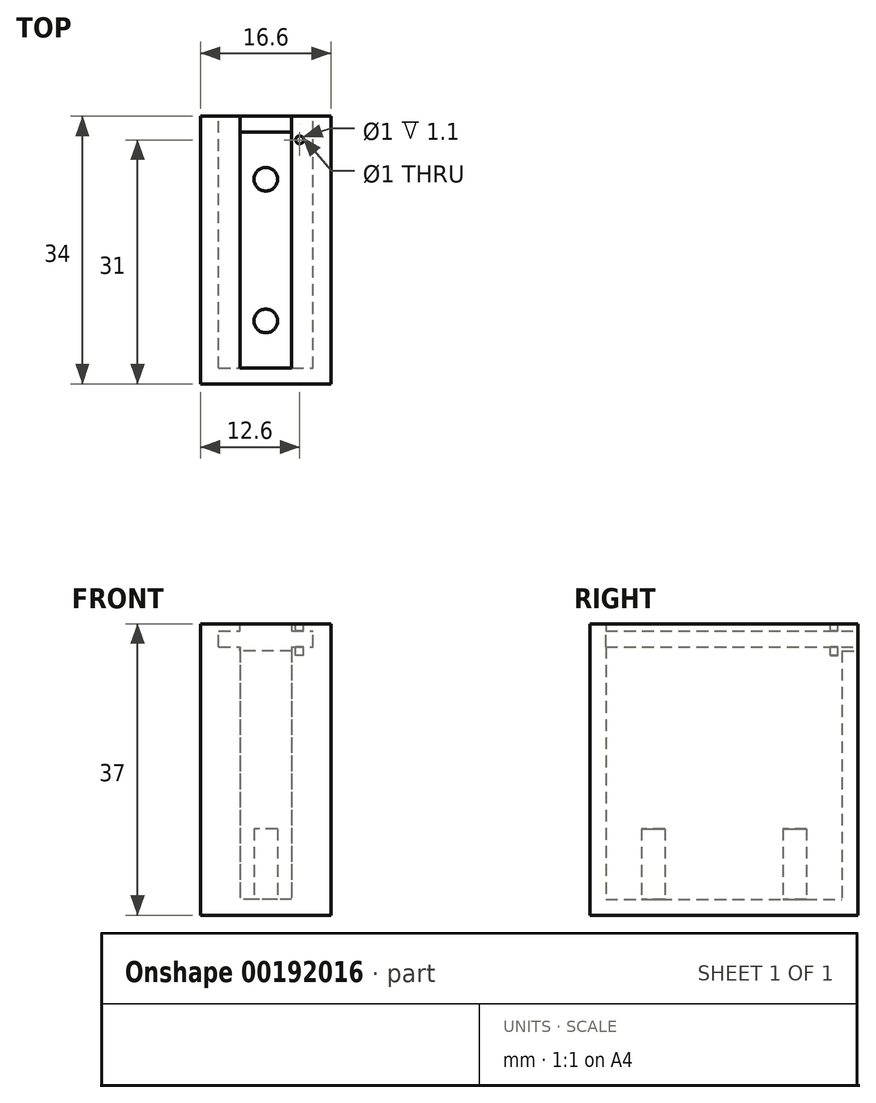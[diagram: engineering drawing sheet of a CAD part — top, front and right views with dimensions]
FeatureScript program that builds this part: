
annotation { "Feature Type Name" : "Feature", "Feature Type Description" : "" }
export const myFeature = defineFeature(function(context is Context, id is Id, definition is map)
    precondition{}
    {
        {
            var Q0;
            Q0=qCreatedBy(makeId("Top.planeOp"),FACE);
            var sketch = newSketch(context, id + "F0", { "sketchPlane" : qUnion([Q0])});
            skLineSegment(sketch, "E0.bottom", {"start": v(3.3, -15) * mm, "end": v(-3.3, -15) * mm});
            skLineSegment(sketch, "E0.top", {"start": v(3.3, 15) * mm, "end": v(-3.3, 15) * mm});
            skLineSegment(sketch, "E0.left", {"start": v(3.3, -15) * mm, "end": v(3.3, 15) * mm});
            skLineSegment(sketch, "E0.right", {"start": v(-3.3, -15) * mm, "end": v(-3.3, 15) * mm});
            skPoint(sketch, "E0.middle", {"position": v(0, 0) * mm});
            skLineSegment(sketch, "E1.bottom", {"start": v(-8.3, 17) * mm, "end": v(8.3, 17) * mm});
            skLineSegment(sketch, "E1.top", {"start": v(-8.3, -17) * mm, "end": v(8.3, -17) * mm});
            skLineSegment(sketch, "E1.left", {"start": v(-8.3, 17) * mm, "end": v(-8.3, -17) * mm});
            skLineSegment(sketch, "E1.right", {"start": v(8.3, 17) * mm, "end": v(8.3, -17) * mm});
            skSolve(sketch);
        }
        {
            var Q0;
            Q0=makeQuery(id+"F0.imprint","IMPRINT",FACE,{"disambiguationData":[TD([[makeQuery(id+"F0.imprint","IMPRINT",EDGE,{"derivedFrom":sQuery(id+"F0.wireOp",EDGE,"E0.bottom")}),-1.0]])]});
            extrude(context, id + "F1", {"entities" : qUnion([Q0]), "depth" : 2 * mm});
        }
        {
            var Q0;
            Q0=makeQuery(id+"F0.imprint","IMPRINT",FACE,{"disambiguationData":[TD([[makeQuery(id+"F0.imprint","IMPRINT",EDGE,{"derivedFrom":sQuery(id+"F0.wireOp",EDGE,"E0.bottom")}),1.0]])]});
            extrude(context, id + "F2", {"entities" : qUnion([Q0]), "operationType" : NewBodyOperationType.ADD, "depth" : (23 + 2 + 9) * mm});
        }
        {
            var Q0;
            Q0=makeQuery(id+"F1.opExtrude","CAP_FACE",FACE,{"disambiguationData":[OSD([sQuery(id+"F0.wireOp",EDGE,"E0.bottom"),sQuery(id+"F0.wireOp",EDGE,"E0.top"),sQuery(id+"F0.wireOp",EDGE,"E0.left"),sQuery(id+"F0.wireOp",EDGE,"E0.right")])],"isStart":false});
            var sketch = newSketch(context, id + "F3", { "sketchPlane" : qUnion([Q0])});
            skCircle(sketch, "E2", {"center": v(0, 9) * mm, "radius": 1.5 * mm});
            skCircle(sketch, "E3", {"center": v(0, -9) * mm, "radius": 1.5 * mm});
            skSolve(sketch);
        }
        {
            var Q0;
            Q0 = qSketchRegion(id + "F3", true);
            extrude(context, id + "F4", {"entities" : qUnion([Q0]), "operationType" : NewBodyOperationType.ADD, "depth" : 9 * mm});
        }
        {
            var Q0;
            Q0=makeQuery(id+"F2.opExtrude","SWEPT_FACE",FACE,{"disambiguationData":[OSD([sQuery(id+"F0.wireOp",EDGE,"E1.bottom")])]});
            var sketch = newSketch(context, id + "F5", { "sketchPlane" : qUnion([Q0])});
            skLineSegment(sketch, "E4", {"start": v(-3.3, 34) * mm, "end": v(-3.3, 33.6) * mm});
            skLineSegment(sketch, "E5", {"start": v(-3.3, 33.6) * mm, "end": v(3.3, 33.6) * mm});
            skLineSegment(sketch, "E6", {"start": v(3.3, 33.6) * mm, "end": v(3.3, 34) * mm});
            skLineSegment(sketch, "E7", {"start": v(3.3, 34) * mm, "end": v(-3.3, 34) * mm});
            skSolve(sketch);
        }
        {
            var Q0;
            Q0 = qSketchRegion(id + "F5", true);
            extrude(context, id + "F6", {"entities" : qUnion([Q0]), "operationType" : NewBodyOperationType.REMOVE, "oppositeDirection" : true, "depth" : 25 * mm});
        }
        {
            var Q0;
            Q0=makeQuery(id+"F2.opExtrude","CAP_FACE",FACE,{"disambiguationData":[OSD([sQuery(id+"F0.wireOp",EDGE,"E0.bottom"),sQuery(id+"F0.wireOp",EDGE,"E0.top"),sQuery(id+"F0.wireOp",EDGE,"E0.left"),sQuery(id+"F0.wireOp",EDGE,"E0.right"),sQuery(id+"F0.wireOp",EDGE,"E1.bottom"),sQuery(id+"F0.wireOp",EDGE,"E1.top"),sQuery(id+"F0.wireOp",EDGE,"E1.left"),sQuery(id+"F0.wireOp",EDGE,"E1.right")])],"isStart":false});
            var sketch = newSketch(context, id + "F7", { "sketchPlane" : qUnion([Q0])});
            skSolve(sketch);
        }
        {
            var Q0;
            {var subQ7=sQuery(id+"F0.wireOp",EDGE,"E0.bottom");Q0=makeQuery(id+"F7.imprint","IMPRINT",FACE,{"disambiguationData":[TD([[makeQuery(id+"F7.imprint","IMPRINT",EDGE,{"derivedFrom":makeQuery(id+"F2.opExtrude","CAP_EDGE",EDGE,{"disambiguationData":[OSD([subQ7])],"isStart":false})}),1.0]])]});}
            extrude(context, id + "F8", {"entities" : qUnion([Q0]), "operationType" : NewBodyOperationType.ADD, "depth" : 3 * mm});
        }
        {
            var Q0;
            {var subQ1=sQuery(id+"F0.wireOp",EDGE,"E1.bottom");var subQ2=makeQuery(id+"F2.opExtrude","SWEPT_FACE",FACE,{"disambiguationData":[OSD([subQ1])]});var subQ3=sQuery(id+"F0.wireOp",EDGE,"E0.left");var subQ5=sQuery(id+"F0.wireOp",EDGE,"E0.right");var subQ7=makeQuery(id+"F2.opExtrude","CAP_EDGE",EDGE,{"disambiguationData":[OSD([subQ1])],"isStart":false});Q0=makeQuery(id+"F8.boolean.opBoolean","MERGE",FACE,{"derivedFrom":[subQ2,makeQuery(id+"F8.opExtrude","SWEPT_FACE",FACE,{"disambiguationData":[OSD([subQ1]),TDD([makeQuery(id+"F7.imprint","IMPRINT",EDGE,{"derivedFrom":makeQuery(id+"F6.boolean.opBoolean","SPLIT",EDGE,{"disambiguationData":[TD([makeQuery(id+"F2.opExtrude","SWEPT_FACE",FACE,{"disambiguationData":[OSD([subQ5])]})])],"derivedFrom":subQ7})})])]}),makeQuery(id+"F8.opExtrude","SWEPT_FACE",FACE,{"disambiguationData":[OSD([subQ1]),TDD([makeQuery(id+"F7.imprint","IMPRINT",EDGE,{"derivedFrom":makeQuery(id+"F6.boolean.opBoolean","SPLIT",EDGE,{"disambiguationData":[TD([makeQuery(id+"F2.opExtrude","SWEPT_FACE",FACE,{"disambiguationData":[OSD([subQ3])]})])],"derivedFrom":subQ7})})])]})]});}
            var sketch = newSketch(context, id + "F9", { "sketchPlane" : qUnion([Q0])});
            skLineSegment(sketch, "E8.bottom", {"start": v(6, 34.1) * mm, "end": v(-6, 34.1) * mm});
            skLineSegment(sketch, "E8.top", {"start": v(6, 36.1) * mm, "end": v(-6, 36.1) * mm});
            skLineSegment(sketch, "E8.left", {"start": v(6, 34.1) * mm, "end": v(6, 36.1) * mm});
            skLineSegment(sketch, "E8.right", {"start": v(-6, 34.1) * mm, "end": v(-6, 36.1) * mm});
            skPoint(sketch, "E8.middle", {"position": v(0, 35.1) * mm});
            skSolve(sketch);
        }
        {
            var Q0;
            Q0 = qSketchRegion(id + "F9", true);
            extrude(context, id + "F10", {"entities" : qUnion([Q0]), "operationType" : NewBodyOperationType.REMOVE, "oppositeDirection" : true, "depth" : 32 * mm});
        }
        {
            var Q0;
            Q0=makeQuery(id+"F8.opExtrude","CAP_FACE",FACE,{"disambiguationData":[OSD([sQuery(id+"F0.wireOp",EDGE,"E0.bottom"),sQuery(id+"F0.wireOp",EDGE,"E0.left"),sQuery(id+"F0.wireOp",EDGE,"E0.right"),sQuery(id+"F0.wireOp",EDGE,"E1.bottom"),sQuery(id+"F0.wireOp",EDGE,"E1.top"),sQuery(id+"F0.wireOp",EDGE,"E1.left"),sQuery(id+"F0.wireOp",EDGE,"E1.right"),sQuery(id+"F5.wireOp",EDGE,"E4"),sQuery(id+"F5.wireOp",EDGE,"E6"),sQuery(id+"F5.wireOp",EDGE,"E7")])],"isStart":false});
            var sketch = newSketch(context, id + "F11", { "sketchPlane" : qUnion([Q0])});
            skCircle(sketch, "E9", {"center": v(4.3, 14) * mm, "radius": 0.5 * mm});
            skSolve(sketch);
        }
        {
            var Q0;
            Q0 = qSketchRegion(id + "F11", true);
            extrude(context, id + "F12", {"entities" : qUnion([Q0]), "operationType" : NewBodyOperationType.REMOVE, "oppositeDirection" : true, "depth" : 4 * mm});
        }
    });
